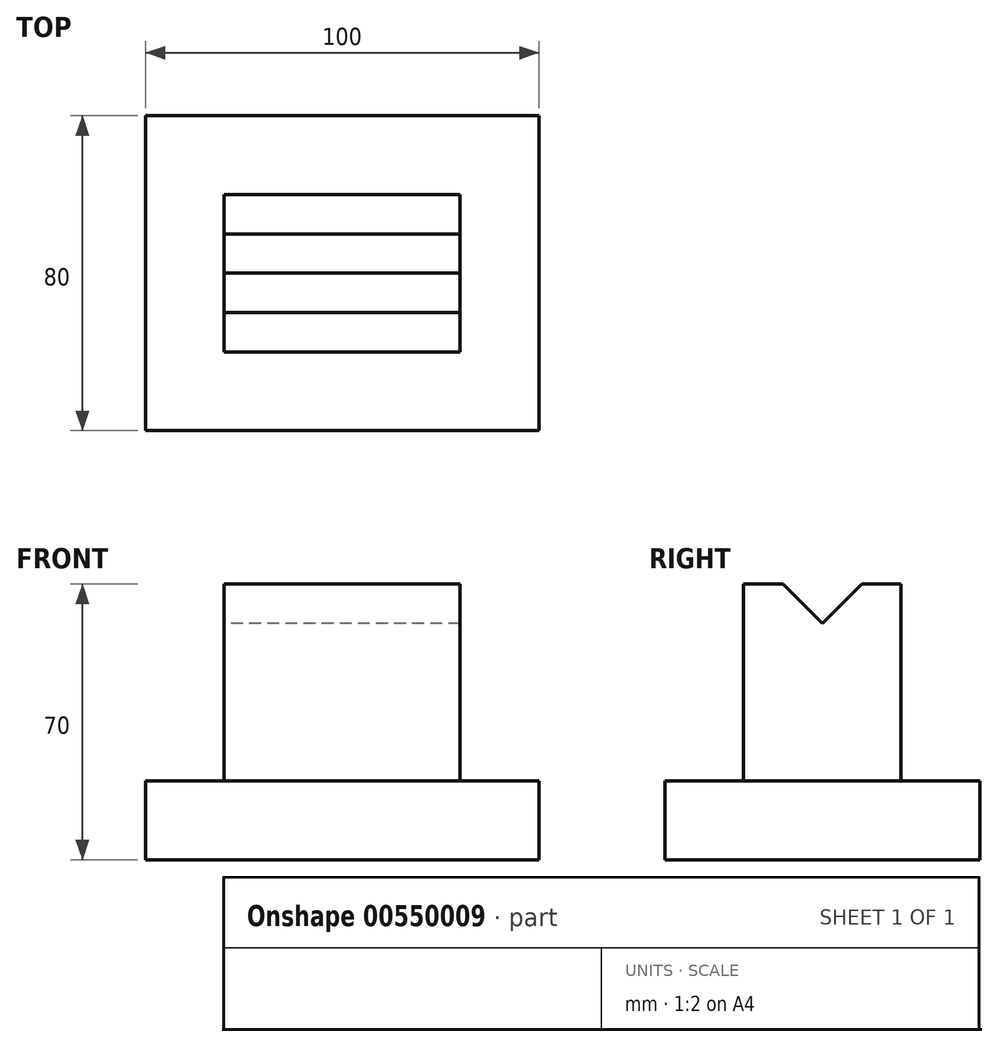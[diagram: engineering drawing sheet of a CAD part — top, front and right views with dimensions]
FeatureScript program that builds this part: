
annotation { "Feature Type Name" : "Feature", "Feature Type Description" : "" }
export const myFeature = defineFeature(function(context is Context, id is Id, definition is map)
    precondition{}
    {
        {
            var Q0;
            Q0=qCreatedBy(makeId("Top.planeOp"),FACE);
            var sketch = newSketch(context, id + "F0", { "sketchPlane" : qUnion([Q0])});
            skLineSegment(sketch, "E0.bottom", {"start": v(50, 40) * mm, "end": v(-50, 40) * mm});
            skLineSegment(sketch, "E0.top", {"start": v(50, -40) * mm, "end": v(-50, -40) * mm});
            skLineSegment(sketch, "E0.left", {"start": v(50, 40) * mm, "end": v(50, -40) * mm});
            skLineSegment(sketch, "E0.right", {"start": v(-50, 40) * mm, "end": v(-50, -40) * mm});
            skPoint(sketch, "E0.middle", {"position": v(0, 0) * mm});
            skSolve(sketch);
        }
        {
            var Q0;
            Q0 = qSketchRegion(id + "F0", true);
            extrude(context, id + "F1", {"entities" : qUnion([Q0]), "depth" : 20 * mm, "offsetDistance" : 25 * mm});
        }
        {
            var Q0;
            Q0=makeQuery(id+"F1.opExtrude","CAP_FACE",FACE,{"disambiguationData":[OSD([sQuery(id+"F0.wireOp",EDGE,"E0.bottom"),sQuery(id+"F0.wireOp",EDGE,"E0.top"),sQuery(id+"F0.wireOp",EDGE,"E0.left"),sQuery(id+"F0.wireOp",EDGE,"E0.right")])],"isStart":false});
            var sketch = newSketch(context, id + "F2", { "sketchPlane" : qUnion([Q0])});
            skLineSegment(sketch, "E1.bottom", {"start": v(30, 20) * mm, "end": v(-30, 20) * mm});
            skLineSegment(sketch, "E1.top", {"start": v(30, -20) * mm, "end": v(-30, -20) * mm});
            skLineSegment(sketch, "E1.left", {"start": v(30, 20) * mm, "end": v(30, -20) * mm});
            skLineSegment(sketch, "E1.right", {"start": v(-30, 20) * mm, "end": v(-30, -20) * mm});
            skPoint(sketch, "E1.middle", {"position": v(0, 0) * mm});
            skSolve(sketch);
        }
        {
            var Q0;
            Q0=makeQuery(id+"F2.imprint","IMPRINT",FACE,{"disambiguationData":[TD([[makeQuery(id+"F2.imprint","IMPRINT",EDGE,{"derivedFrom":sQuery(id+"F2.wireOp",EDGE,"E1.bottom")}),1.0]])]});
            extrude(context, id + "F3", {"entities" : qUnion([Q0]), "operationType" : NewBodyOperationType.ADD, "depth" : 50 * mm, "offsetDistance" : 25 * mm});
        }
        {
            var Q0;
            Q0=makeQuery(id+"F3.opExtrude","SWEPT_FACE",FACE,{"disambiguationData":[OSD([sQuery(id+"F2.wireOp",EDGE,"E1.right")])]});
            var sketch = newSketch(context, id + "F4", { "sketchPlane" : qUnion([Q0])});
            skLineSegment(sketch, "E2", {"start": v(-20, 70) * mm, "end": v(-10, 70) * mm});
            skLineSegment(sketch, "E3", {"start": v(-10, 70) * mm, "end": v(10, 70) * mm});
            skLineSegment(sketch, "E4", {"start": v(10, 70) * mm, "end": v(20, 70) * mm});
            skLineSegment(sketch, "E5", {"start": v(-10, 70) * mm, "end": v(0, 60) * mm});
            skLineSegment(sketch, "E6", {"start": v(10, 70) * mm, "end": v(0, 60) * mm});
            skSolve(sketch);
        }
        {
            var Q0;
            Q0 = qSketchRegion(id + "F4", true);
            extrude(context, id + "F5", {"entities" : qUnion([Q0]), "operationType" : NewBodyOperationType.REMOVE, "oppositeDirection" : true, "depth" : 81 * mm, "offsetDistance" : 25 * mm});
        }
    });
